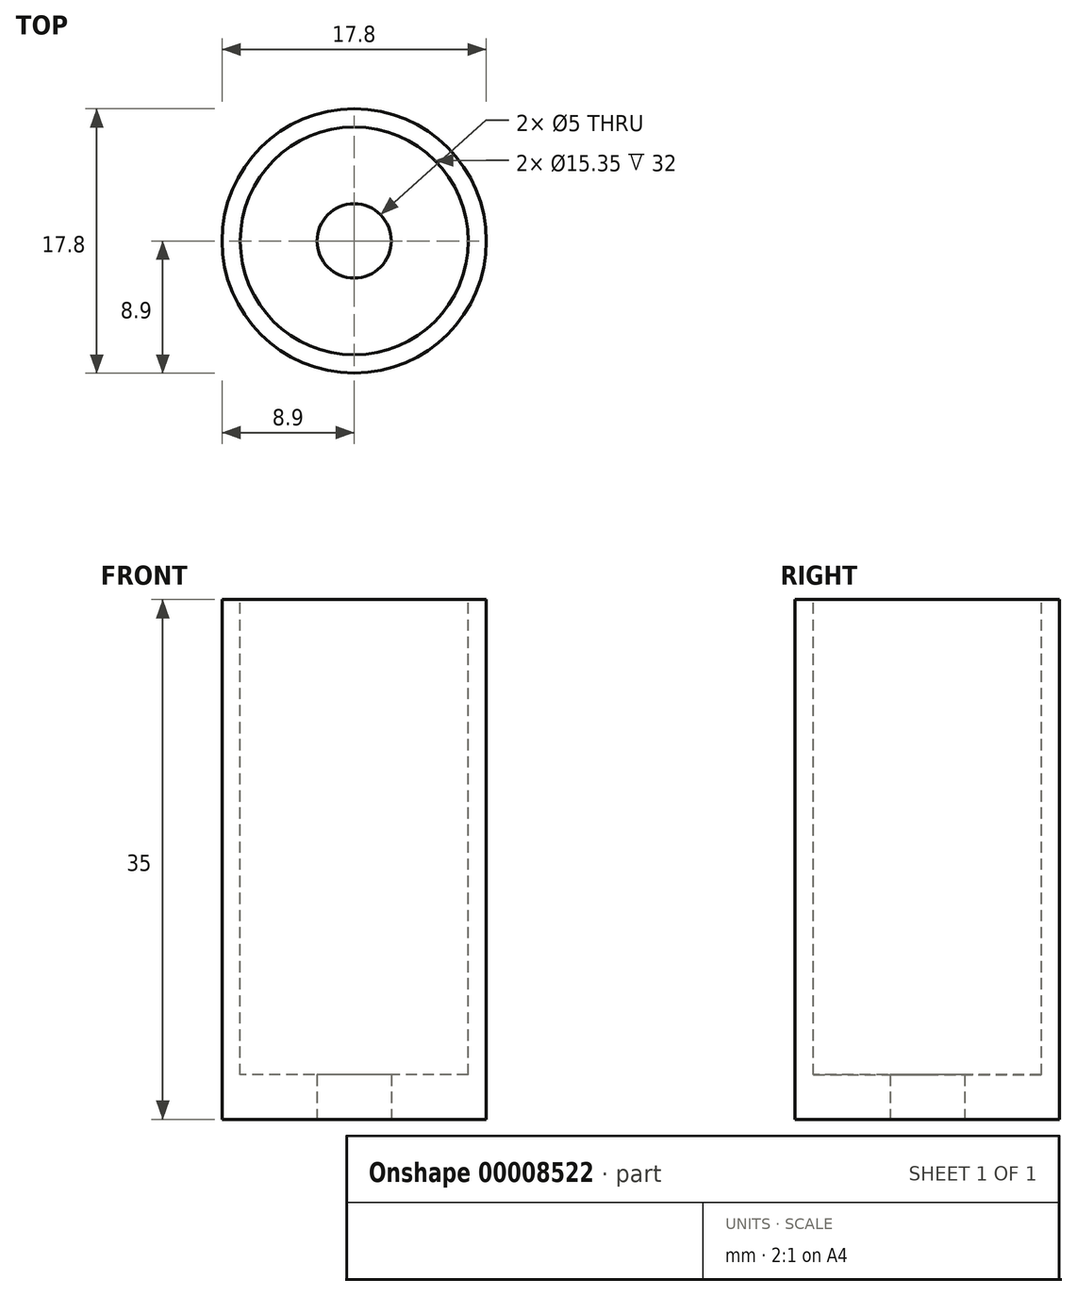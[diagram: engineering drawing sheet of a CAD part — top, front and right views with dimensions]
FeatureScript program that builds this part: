
annotation { "Feature Type Name" : "Feature", "Feature Type Description" : "" }
export const myFeature = defineFeature(function(context is Context, id is Id, definition is map)
    precondition{}
    {
        {
            var Q0;
            Q0=qCreatedBy(makeId("Top.planeOp"),FACE);
            var sketch = newSketch(context, id + "F0", { "sketchPlane" : qUnion([Q0])});
            skCircle(sketch, "E0", {"center": v(0, 0) * mm, "radius": 8.9 * mm});
            skCircle(sketch, "E1", {"center": v(0, 0) * mm, "radius": 2.5 * mm});
            skSolve(sketch);
        }
        {
            var Q0;
            Q0 = qSketchRegion(id + "F0", true);
            extrude(context, id + "F1", {"entities" : qUnion([Q0]), "depth" : 35 * mm});
        }
        {
            var Q0;
            Q0=makeQuery(id+"F1.opExtrude","CAP_FACE",FACE,{"disambiguationData":[OSD([sQuery(id+"F0.wireOp",EDGE,"E0"),sQuery(id+"F0.wireOp",EDGE,"E1")])],"isStart":false});
            var sketch = newSketch(context, id + "F2", { "sketchPlane" : qUnion([Q0])});
            skCircle(sketch, "E2", {"center": v(0, 0) * mm, "radius": 7.68 * mm});
            skSolve(sketch);
        }
        {
            var Q0;
            Q0 = qSketchRegion(id + "F2", true);
            extrude(context, id + "F3", {"entities" : qUnion([Q0]), "operationType" : NewBodyOperationType.REMOVE, "oppositeDirection" : true, "depth" : 32 * mm});
        }
    });
